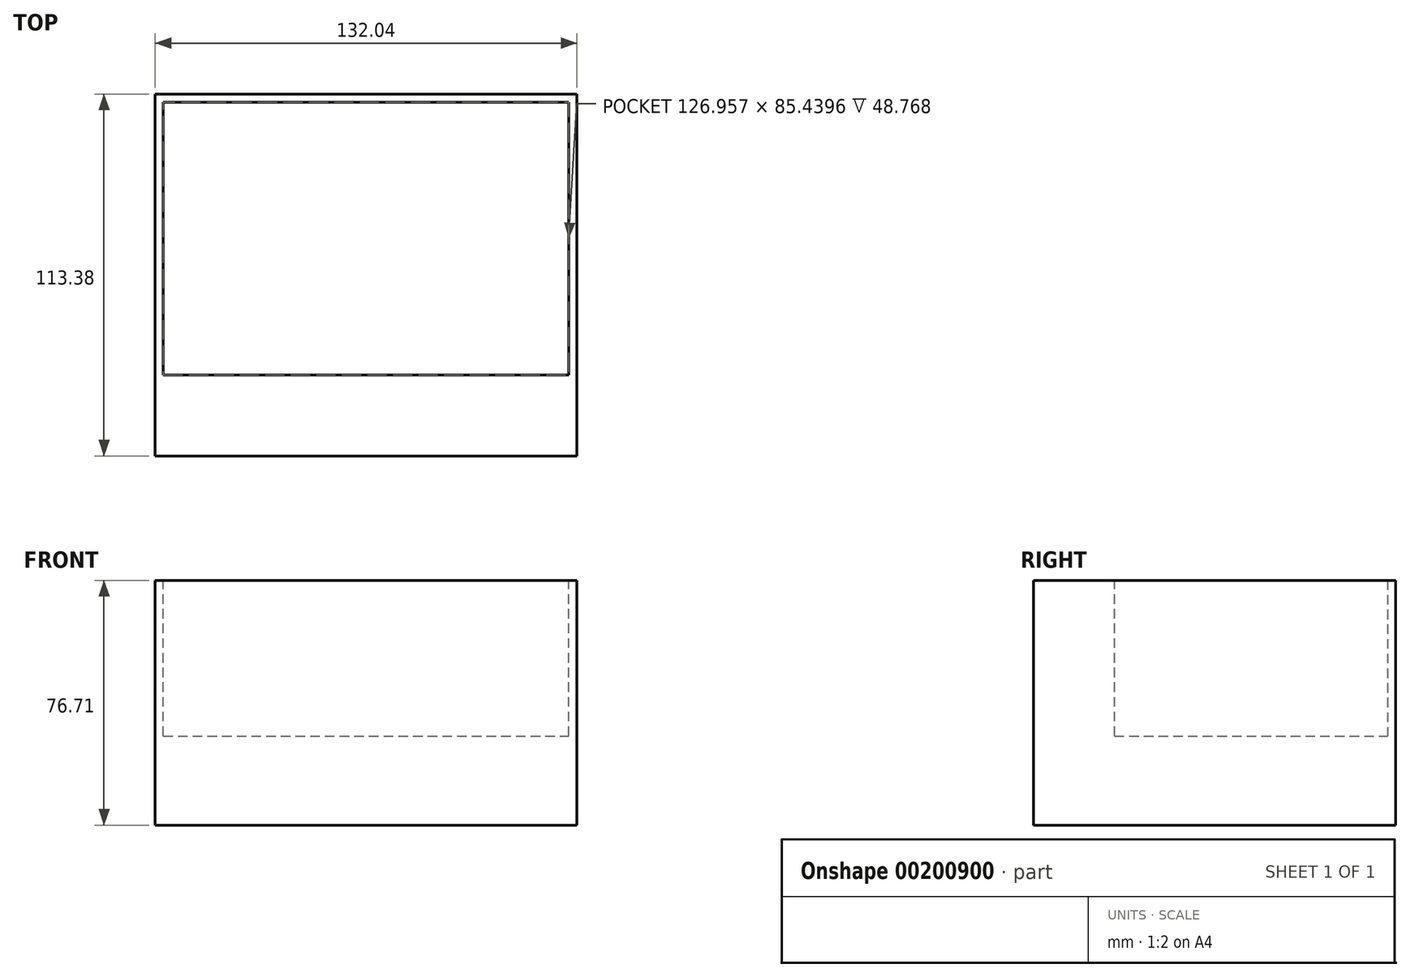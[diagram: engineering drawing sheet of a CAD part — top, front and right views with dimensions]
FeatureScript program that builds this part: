
annotation { "Feature Type Name" : "Feature", "Feature Type Description" : "" }
export const myFeature = defineFeature(function(context is Context, id is Id, definition is map)
    precondition{}
    {
        {
            var Q0;
            Q0=qCreatedBy(makeId("Top.planeOp"),FACE);
            var sketch = newSketch(context, id + "F0", { "sketchPlane" : qUnion([Q0])});
            skLineSegment(sketch, "E0.bottom", {"start": v(66.02, -56.69) * mm, "end": v(-66.02, -56.69) * mm});
            skLineSegment(sketch, "E0.top", {"start": v(66.02, 56.69) * mm, "end": v(-66.02, 56.69) * mm});
            skLineSegment(sketch, "E0.left", {"start": v(66.02, -56.69) * mm, "end": v(66.02, 56.69) * mm});
            skLineSegment(sketch, "E0.right", {"start": v(-66.02, -56.69) * mm, "end": v(-66.02, 56.69) * mm});
            skPoint(sketch, "E0.middle", {"position": v(0, 0) * mm});
            skSolve(sketch);
        }
        {
            var Q0;
            Q0=makeQuery(id+"F0.imprint","IMPRINT",FACE,{"disambiguationData":[TD([[makeQuery(id+"F0.imprint","IMPRINT",EDGE,{"derivedFrom":sQuery(id+"F0.wireOp",EDGE,"E0.bottom")}),-1.0]])]});
            extrude(context, id + "F1", {"entities" : qUnion([Q0]), "depth" : 76.7 * mm});
        }
        {
            var Q0;
            Q0=makeQuery(id+"F1.opExtrude","CAP_FACE",FACE,{"disambiguationData":[OSD([sQuery(id+"F0.wireOp",EDGE,"E0.bottom"),sQuery(id+"F0.wireOp",EDGE,"E0.top"),sQuery(id+"F0.wireOp",EDGE,"E0.left"),sQuery(id+"F0.wireOp",EDGE,"E0.right")])],"isStart":false});
            shell(context, id + "F2", {"entities" : qUnion([Q0]), "thickness" : 2.54 * mm});
        }
        {
            var Q0;
            Q0=makeQuery(id+"F2.opShell","OFFSET_FACE",FACE,{"disambiguationData":[OSD([sQuery(id+"F0.wireOp",EDGE,"E0.bottom"),sQuery(id+"F0.wireOp",EDGE,"E0.top"),sQuery(id+"F0.wireOp",EDGE,"E0.left"),sQuery(id+"F0.wireOp",EDGE,"E0.right")])]});
            extrude(context, id + "F3", {"entities" : qUnion([Q0]), "operationType" : NewBodyOperationType.ADD, "depth" : 25.4 * mm});
        }
        {
            var Q0;
            Q0=makeQuery(id+"F1.opExtrude","SWEPT_FACE",FACE,{"disambiguationData":[OSD([sQuery(id+"F0.wireOp",EDGE,"E0.bottom")])]});
            extrude(context, id + "F4", {"entities" : qUnion([Q0]), "operationType" : NewBodyOperationType.ADD, "oppositeDirection" : true, "depth" : 25.4 * mm});
        }
    });
